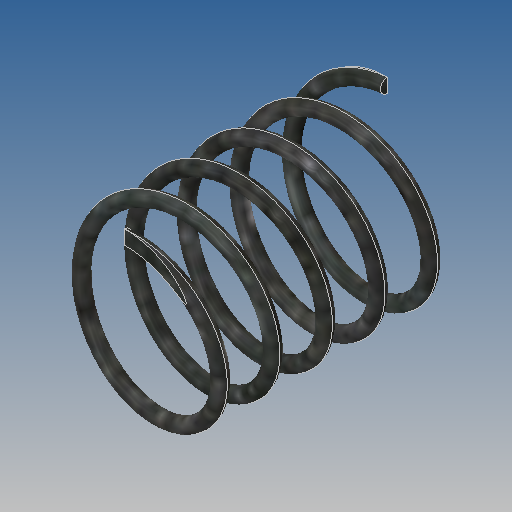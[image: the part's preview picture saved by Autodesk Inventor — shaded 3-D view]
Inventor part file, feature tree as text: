
AUTODESK INVENTOR PART (.ipt)
format: ipt  version: 2019 (Build 230136000, 136)  size: 339,968 bytes
history: native  units: mm
features: sketch x2, other x1, extrude x1, projected_geometry x1
ambient origin geometry x8: Origin, YZ Plane, XZ Plane, XY Plane, X Axis, Y Axis, Z Axis, Center Point
bodies: Solide1 (feature_tree)
feature tree (5):
  other  "Hélicoïde1"
  extrude  "Extrusion1"  Depth=1.5mm
  sketch  "Esquisse1"
  sketch  "Esquisse2"
  projected_geometry  "Boucle projetée1"
